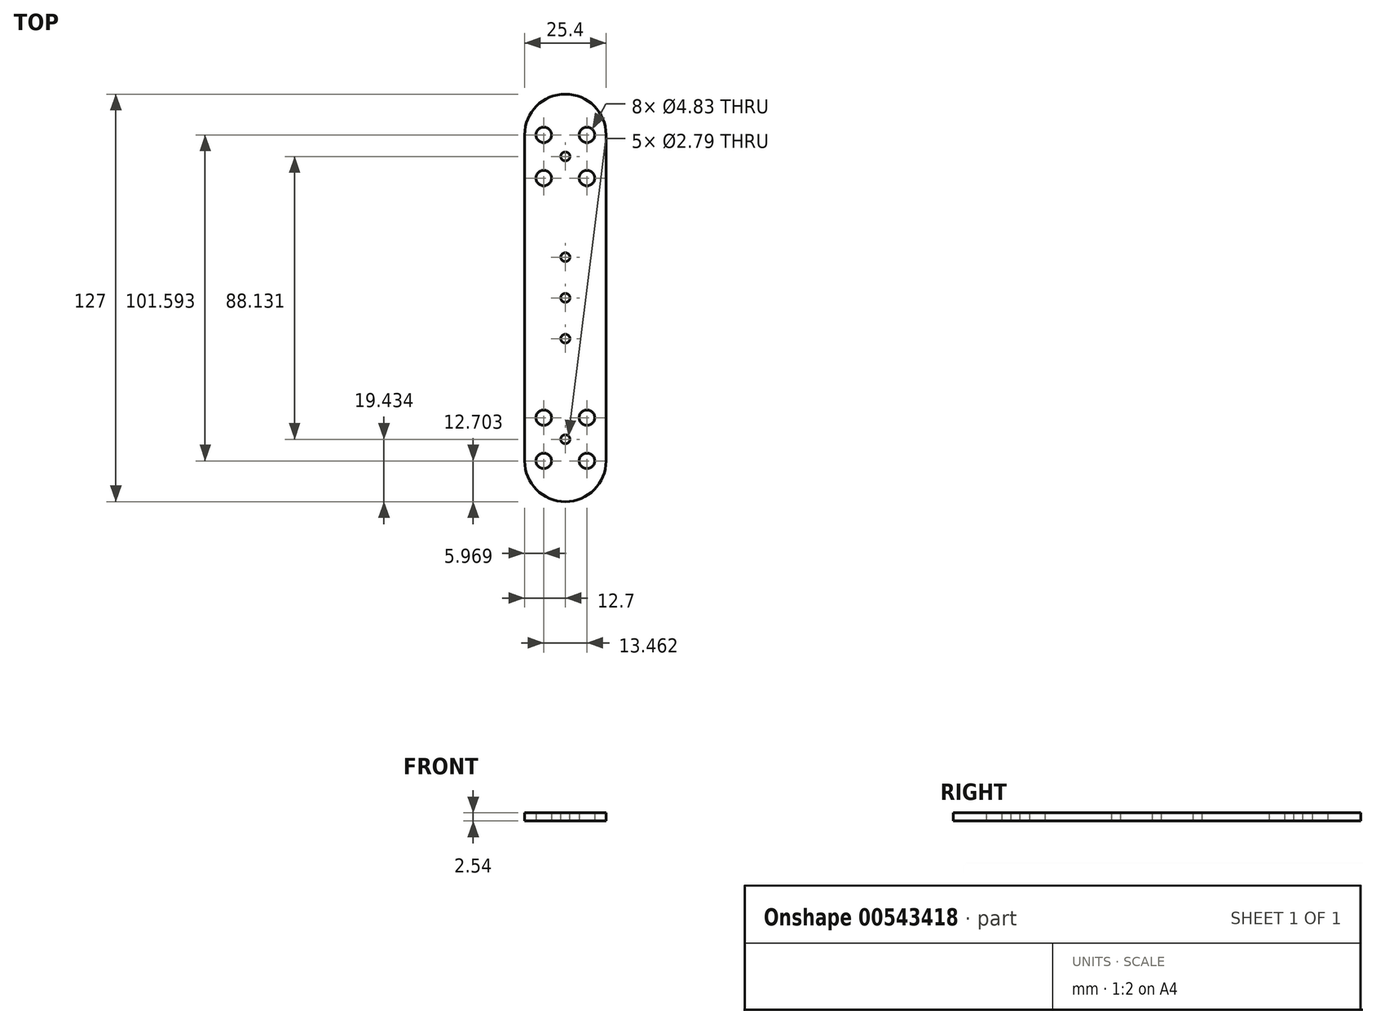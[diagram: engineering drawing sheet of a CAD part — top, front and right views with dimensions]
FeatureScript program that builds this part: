
annotation { "Feature Type Name" : "Feature", "Feature Type Description" : "" }
export const myFeature = defineFeature(function(context is Context, id is Id, definition is map)
    precondition{}
    {
        {
            var Q0;
            Q0=qCreatedBy(makeId("Top.planeOp"),FACE);
            var sketch = newSketch(context, id + "F0", { "sketchPlane" : qUnion([Q0])});
            skLineSegment(sketch, "E0.left", {"start": v(12.7, 50.8) * mm, "end": v(12.7, -50.8) * mm});
            skLineSegment(sketch, "E0.right", {"start": v(-12.7, 50.8) * mm, "end": v(-12.7, -50.8) * mm});
            skPoint(sketch, "E0.middle", {"position": v(0, 0) * mm});
            skLineSegment(sketch, "E1.bottom", {"start": v(6.73, -50.8) * mm, "end": v(-6.73, -50.8) * mm});
            skLineSegment(sketch, "E1.top", {"start": v(6.73, -37.33) * mm, "end": v(-6.73, -37.33) * mm});
            skLineSegment(sketch, "E1.left", {"start": v(6.73, -50.8) * mm, "end": v(6.73, -37.33) * mm});
            skLineSegment(sketch, "E1.right", {"start": v(-6.73, -50.8) * mm, "end": v(-6.73, -37.33) * mm});
            skPoint(sketch, "E1.middle", {"position": v(0, -44.07) * mm});
            skCircle(sketch, "E2", {"center": v(-6.73, -37.33) * mm, "radius": 2.41 * mm});
            skCircle(sketch, "E3", {"center": v(6.73, -37.33) * mm, "radius": 2.41 * mm});
            skCircle(sketch, "E4", {"center": v(6.73, -50.8) * mm, "radius": 2.41 * mm});
            skCircle(sketch, "E5", {"center": v(-6.73, -50.8) * mm, "radius": 2.41 * mm});
            skArc(sketch, "E6", {"start": v(-12.7, -50.8) * mm, "mid": v(0, -63.5) * mm, "end": v(12.7, -50.8) * mm});
            skArc(sketch, "E7", {"start": v(12.7, 50.8) * mm, "mid": v(0, 63.5) * mm, "end": v(-12.7, 50.8) * mm});
            skLineSegment(sketch, "E8", {"start": v(-8.67, 0) * mm, "end": v(8.23, 0) * mm});
            skCircle(sketch, "E9.MirrorC", {"center": v(-6.73, 37.33) * mm, "radius": 2.41 * mm});
            skCircle(sketch, "E10.MirrorC", {"center": v(6.73, 37.33) * mm, "radius": 2.41 * mm});
            skCircle(sketch, "E11.MirrorC", {"center": v(-6.73, 50.8) * mm, "radius": 2.41 * mm});
            skCircle(sketch, "E12.MirrorC", {"center": v(6.73, 50.8) * mm, "radius": 2.41 * mm});
            skSolve(sketch);
        }
        {
            var Q0;
            Q0=qSketchRegion(id+"F0",true);
            var Q1;
            {var subQ5=sQuery(id+"F0.wireOp",EDGE,"E4");var subQ10=sQuery(id+"F0.wireOp",EDGE,"E1.bottom");var subQ15=makeQuery(id+"F0.imprint","INTERSECT",VERTEX,{"derivedFrom":[subQ10,subQ5]});Q1=makeQuery(id+"F0.imprint","IMPRINT",FACE,{"disambiguationData":[TD([[makeQuery(id+"F0.imprint","IMPRINT",EDGE,{"disambiguationData":[TD([[subQ15,-1.0]])],"derivedFrom":subQ10}),-1.0]])]});}
            extrude(context, id + "F1", {"entities" : qUnion([Q0, Q1]), "depth" : 2.54 * mm, "offsetDistance" : 25.4 * mm});
        }
        {
            var Q0;
            Q0=makeQuery(id+"F1.opExtrude","CAP_FACE",FACE,{"disambiguationData":[OSD([sQuery(id+"F0.wireOp",EDGE,"E0.left"),sQuery(id+"F0.wireOp",EDGE,"E0.right"),sQuery(id+"F0.wireOp",EDGE,"E2"),sQuery(id+"F0.wireOp",EDGE,"E3"),sQuery(id+"F0.wireOp",EDGE,"E4"),sQuery(id+"F0.wireOp",EDGE,"E5"),sQuery(id+"F0.wireOp",EDGE,"E6"),sQuery(id+"F0.wireOp",EDGE,"E7")])],"isStart":false});
            var sketch = newSketch(context, id + "F2", { "sketchPlane" : qUnion([Q0])});
            skCircle(sketch, "E13", {"center": v(0, 0) * mm, "radius": 1.4 * mm});
            skLineSegment(sketch, "E14", {"start": v(-6.73, 50.8) * mm, "end": v(6.73, 37.33) * mm});
            skLineSegment(sketch, "E15", {"start": v(6.73, 50.8) * mm, "end": v(-6.73, 37.33) * mm});
            skCircle(sketch, "E16", {"center": v(0, 44.07) * mm, "radius": 1.4 * mm});
            skCircle(sketch, "E17.MirrorC", {"center": v(0, -44.07) * mm, "radius": 1.4 * mm});
            skLineSegment(sketch, "E18", {"start": v(0, 13.87) * mm, "end": v(0, -13.8) * mm});
            skCircle(sketch, "E19", {"center": v(0, 12.69) * mm, "radius": 1.4 * mm});
            skCircle(sketch, "E20", {"center": v(0, -12.71) * mm, "radius": 1.4 * mm});
            skPoint(sketch, "E21", {"position": v(0, -0.01) * mm});
            skSolve(sketch);
        }
        {
            var Q0;
            Q0=qSketchRegion(id+"F2",true);
            extrude(context, id + "F3", {"entities" : qUnion([Q0]), "operationType" : NewBodyOperationType.REMOVE, "endBound" : BoundingType.THROUGH_ALL, "oppositeDirection" : true, "depth" : 6.35 * mm, "offsetDistance" : 25.4 * mm});
        }
    });
